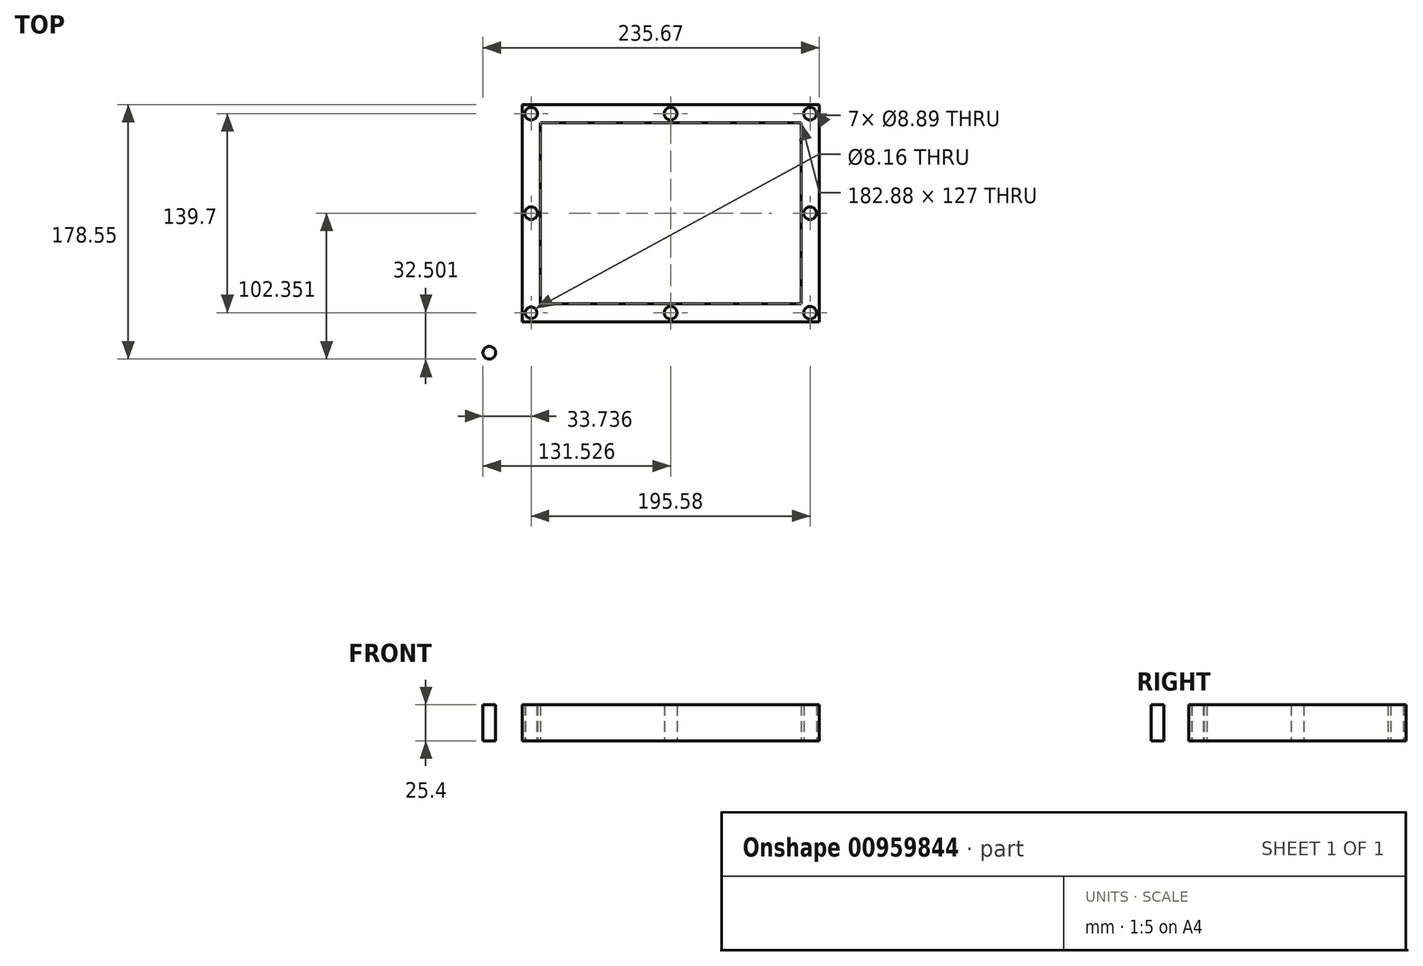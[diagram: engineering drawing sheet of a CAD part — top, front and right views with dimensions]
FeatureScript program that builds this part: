
annotation { "Feature Type Name" : "Feature", "Feature Type Description" : "" }
export const myFeature = defineFeature(function(context is Context, id is Id, definition is map)
    precondition{}
    {
        {
            var Q0;
            Q0=qCreatedBy(makeId("Top.planeOp"),FACE);
            var sketch = newSketch(context, id + "F0", { "sketchPlane" : qUnion([Q0])});
            skLineSegment(sketch, "E0.bottom", {"start": v(-98.3, 89.75) * mm, "end": v(109.99, 89.75) * mm});
            skLineSegment(sketch, "E0.top", {"start": v(-98.3, -62.65) * mm, "end": v(109.99, -62.65) * mm});
            skLineSegment(sketch, "E0.left", {"start": v(-98.3, 89.75) * mm, "end": v(-98.3, -62.65) * mm});
            skLineSegment(sketch, "E0.right", {"start": v(109.99, 89.75) * mm, "end": v(109.99, -62.65) * mm});
            skLineSegment(sketch, "E1.bottom", {"start": v(-85.6, 77.05) * mm, "end": v(97.29, 77.05) * mm});
            skLineSegment(sketch, "E1.top", {"start": v(-85.6, -49.95) * mm, "end": v(97.29, -49.95) * mm});
            skLineSegment(sketch, "E1.left", {"start": v(-85.6, 77.05) * mm, "end": v(-85.6, -49.95) * mm});
            skLineSegment(sketch, "E1.right", {"start": v(97.29, 77.05) * mm, "end": v(97.29, -49.95) * mm});
            skLineSegment(sketch, "E2", {"start": v(97.29, 77.05) * mm, "end": v(109.99, 77.05) * mm, "construction": true});
            skLineSegment(sketch, "E3", {"start": v(-85.6, -49.95) * mm, "end": v(-85.6, -62.65) * mm, "construction": true});
            skLineSegment(sketch, "E4", {"start": v(-85.6, -56.3) * mm, "end": v(-98.3, -56.3) * mm});
            skLineSegment(sketch, "E5", {"start": v(-98.3, -56.3) * mm, "end": v(109.99, -56.3) * mm, "construction": true});
            skLineSegment(sketch, "E6", {"start": v(-91.94, -56.3) * mm, "end": v(-91.94, 89.75) * mm, "construction": true});
            skLineSegment(sketch, "E7", {"start": v(42.5, 77.05) * mm, "end": v(42.5, 89.75) * mm, "construction": true});
            skLineSegment(sketch, "E8", {"start": v(-91.94, 83.4) * mm, "end": v(109.99, 83.4) * mm, "construction": true});
            skLineSegment(sketch, "E9", {"start": v(97.29, 13.55) * mm, "end": v(109.99, 13.55) * mm, "construction": true});
            skLineSegment(sketch, "E10", {"start": v(103.64, 13.55) * mm, "end": v(103.64, 83.4) * mm, "construction": true});
            skLineSegment(sketch, "E11", {"start": v(103.64, 13.55) * mm, "end": v(103.64, -56.3) * mm, "construction": true});
            skLineSegment(sketch, "E12", {"start": v(97.29, -49.95) * mm, "end": v(109.99, -49.95) * mm});
            skLineSegment(sketch, "E13", {"start": v(97.29, -49.95) * mm, "end": v(97.29, -62.65) * mm});
            skLineSegment(sketch, "E14", {"start": v(97.28, 89.75) * mm, "end": v(97.29, 77.05) * mm});
            skLineSegment(sketch, "E15", {"start": v(-85.65, -49.95) * mm, "end": v(-85.6, -62.65) * mm});
            skLineSegment(sketch, "E16", {"start": v(-85.6, -49.95) * mm, "end": v(-98.3, -49.95) * mm});
            skLineSegment(sketch, "E17", {"start": v(-85.6, 77.05) * mm, "end": v(-85.6, 89.75) * mm});
            skLineSegment(sketch, "E18", {"start": v(-85.6, 77.05) * mm, "end": v(-98.3, 77.05) * mm});
            skLineSegment(sketch, "E19", {"start": v(5.85, 89.75) * mm, "end": v(5.85, -62.65) * mm, "construction": true});
            skCircle(sketch, "E20", {"center": v(-121.23, -84.36) * mm, "radius": 4.45 * mm});
            skLineSegment(sketch, "E21", {"start": v(-121.23, -84.36) * mm, "end": v(-121.23, -79.91) * mm, "construction": true});
            skCircle(sketch, "E22", {"center": v(-91.94, -56.3) * mm, "radius": 4.08 * mm});
            skCircle(sketch, "E23", {"center": v(103.64, 83.4) * mm, "radius": 4.45 * mm});
            skCircle(sketch, "E24", {"center": v(103.64, 13.55) * mm, "radius": 4.45 * mm});
            skCircle(sketch, "E25", {"center": v(103.64, -56.3) * mm, "radius": 4.45 * mm});
            skCircle(sketch, "E26", {"center": v(5.85, -56.3) * mm, "radius": 4.45 * mm});
            skCircle(sketch, "E27", {"center": v(-91.94, 83.4) * mm, "radius": 4.45 * mm});
            skCircle(sketch, "E28", {"center": v(5.85, 83.4) * mm, "radius": 4.45 * mm});
            skCircle(sketch, "E29", {"center": v(-91.94, 13.55) * mm, "radius": 4.45 * mm});
            skPoint(sketch, "E29.perimeterSnap0", {"position": v(-85.6, 13.55) * mm});
            skPoint(sketch, "E29.perimeterSnap1", {"position": v(-91.94, 16.73) * mm});
            skSolve(sketch);
        }
        {
            var Q0;
            Q0 = qSketchRegion(id + "F0", true);
            extrude(context, id + "F1", {"entities" : qUnion([Q0]), "depth" : 25.4 * mm, "offsetDistance" : 25.4 * mm});
        }
    });
